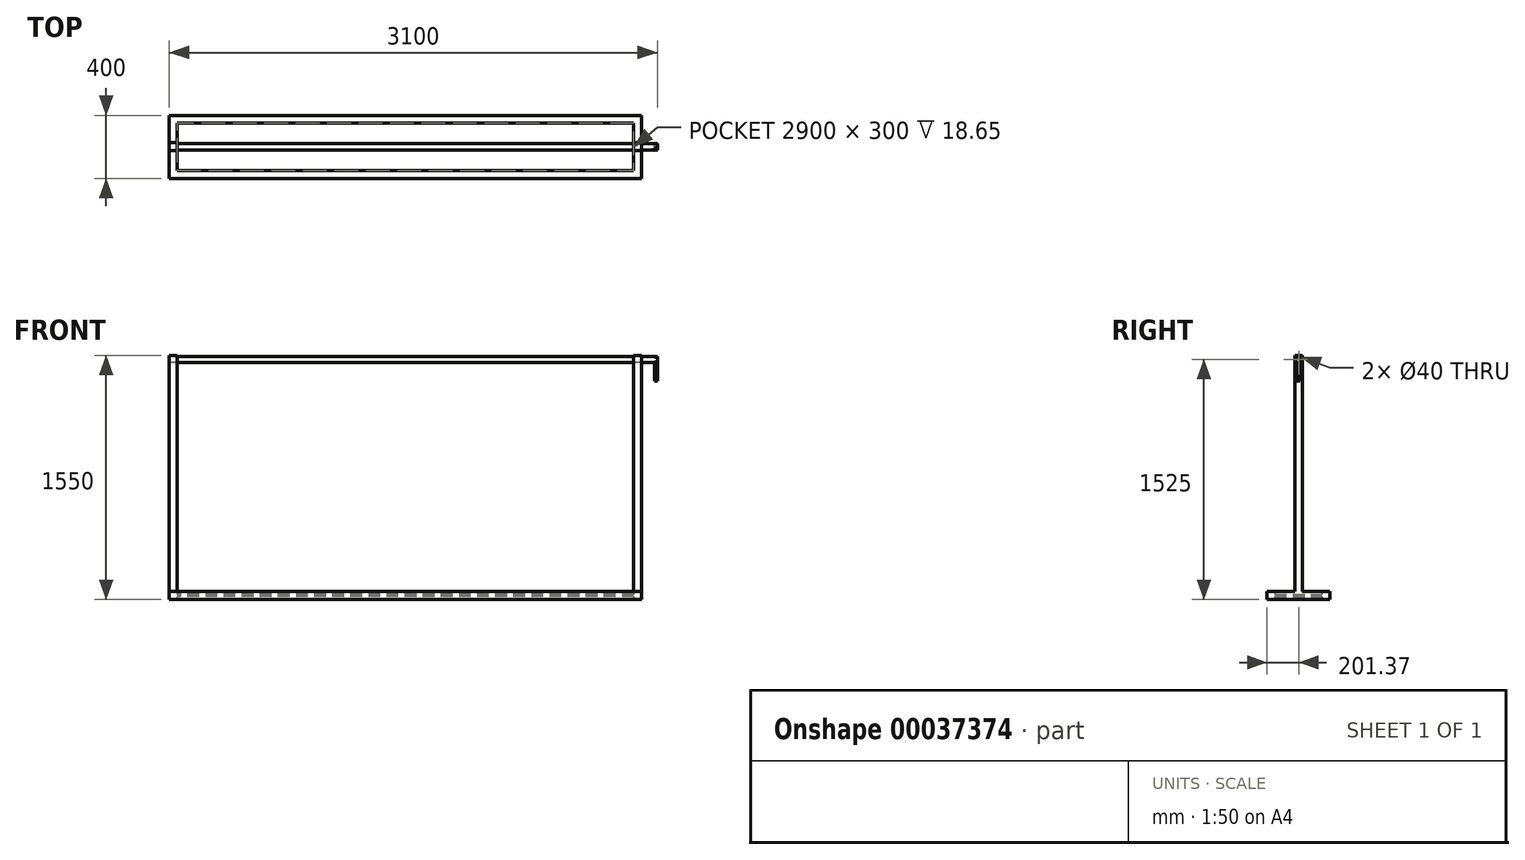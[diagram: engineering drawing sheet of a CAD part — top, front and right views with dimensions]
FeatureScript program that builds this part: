
annotation { "Feature Type Name" : "Feature", "Feature Type Description" : "" }
export const myFeature = defineFeature(function(context is Context, id is Id, definition is map)
    precondition{}
    {
        {
            var Q0;
            Q0=qCreatedBy(makeId("Top.planeOp"),FACE);
            var sketch = newSketch(context, id + "F0", { "sketchPlane" : qUnion([Q0])});
            skLineSegment(sketch, "E0.rect.bottom", {"start": v(1500, -200) * mm, "end": v(-1500, -200) * mm});
            skLineSegment(sketch, "E0.rect.top", {"start": v(1500, 200) * mm, "end": v(-1500, 200) * mm});
            skLineSegment(sketch, "E0.rect.left", {"start": v(1500, -200) * mm, "end": v(1500, 200) * mm});
            skLineSegment(sketch, "E0.rect.right", {"start": v(-1500, -200) * mm, "end": v(-1500, 200) * mm});
            skPoint(sketch, "E0.rect.middle", {"position": v(0, 0) * mm});
            skLineSegment(sketch, "E1.0", {"start": v(1450, -150) * mm, "end": v(-1450, -150) * mm});
            skLineSegment(sketch, "E2.0", {"start": v(-1450, -150) * mm, "end": v(-1450, 150) * mm});
            skLineSegment(sketch, "E3.0", {"start": v(1450, 150) * mm, "end": v(-1450, 150) * mm});
            skLineSegment(sketch, "E4.0", {"start": v(1450, -150) * mm, "end": v(1450, 150) * mm});
            skSolve(sketch);
        }
        {
            var Q0;
            Q0 = qSketchRegion(id + "F0", true);
            extrude(context, id + "F1", {"entities" : qUnion([Q0]), "endBound" : BoundingType.SYMMETRIC, "depth" : 50 * mm});
        }
        {
            var Q0;
            Q0=makeQuery(id+"F1.opExtrude","CAP_FACE",FACE,{"disambiguationData":[OSD([sQuery(id+"F0.wireOp",EDGE,"E0.rect.bottom"),sQuery(id+"F0.wireOp",EDGE,"E0.rect.top"),sQuery(id+"F0.wireOp",EDGE,"E0.rect.left"),sQuery(id+"F0.wireOp",EDGE,"E0.rect.right"),sQuery(id+"F0.wireOp",EDGE,"E1.0"),sQuery(id+"F0.wireOp",EDGE,"E2.0"),sQuery(id+"F0.wireOp",EDGE,"E3.0"),sQuery(id+"F0.wireOp",EDGE,"E4.0")])],"isStart":false});
            var sketch = newSketch(context, id + "F2", { "sketchPlane" : qUnion([Q0])});
            skPoint(sketch, "E5.MirrorP", {"position": v(1500, 0) * mm});
            skLineSegment(sketch, "E6", {"start": v(-1500, 0) * mm, "end": v(-1500, 26.37) * mm});
            skLineSegment(sketch, "E7.bottom", {"start": v(-1500, 26.37) * mm, "end": v(-1450, 26.37) * mm});
            skLineSegment(sketch, "E7.top", {"start": v(-1500, -23.63) * mm, "end": v(-1450, -23.63) * mm});
            skLineSegment(sketch, "E7.left", {"start": v(-1500, 26.37) * mm, "end": v(-1500, -23.63) * mm});
            skLineSegment(sketch, "E7.right", {"start": v(-1450, 26.37) * mm, "end": v(-1450, -23.63) * mm});
            skLineSegment(sketch, "E8.MirrorCS", {"start": v(1500, 0) * mm, "end": v(1500, 26.37) * mm});
            skLineSegment(sketch, "E9.MirrorCS", {"start": v(1500, 26.37) * mm, "end": v(1450, 26.37) * mm});
            skLineSegment(sketch, "E10.MirrorCS", {"start": v(1450, 26.37) * mm, "end": v(1450, -23.63) * mm});
            skLineSegment(sketch, "E11.MirrorCS", {"start": v(1500, -23.63) * mm, "end": v(1450, -23.63) * mm});
            skLineSegment(sketch, "E12.MirrorCS", {"start": v(1500, 26.37) * mm, "end": v(1500, -23.63) * mm});
            skSolve(sketch);
        }
        {
            var Q0;
            Q0 = qSketchRegion(id + "F2", true);
            extrude(context, id + "F3", {"entities" : qUnion([Q0]), "operationType" : NewBodyOperationType.ADD, "depth" : 1500 * mm});
        }
        {
            var Q0;
            Q0=makeQuery(id+"F3.boolean.opBoolean","MERGE",FACE,{"derivedFrom":[makeQuery(id+"F1.opExtrude","SWEPT_FACE",FACE,{"disambiguationData":[OSD([sQuery(id+"F0.wireOp",EDGE,"E0.rect.right")])]}),makeQuery(id+"F3.opExtrude","SWEPT_FACE",FACE,{"disambiguationData":[OSD([sQuery(id+"F2.wireOp",EDGE,"E7.left")])]})]});
            var sketch = newSketch(context, id + "F4", { "sketchPlane" : qUnion([Q0])});
            skCircle(sketch, "E13", {"center": v(-1.37, 1500) * mm, "radius": 20 * mm});
            skSolve(sketch);
        }
        {
            var Q0;
            Q0 = qSketchRegion(id + "F4", true);
            extrude(context, id + "F5", {"entities" : qUnion([Q0]), "operationType" : NewBodyOperationType.REMOVE, "oppositeDirection" : true, "depth" : 3064.82 * mm});
        }
        {
            var Q0;
            Q0=makeQuery(id+"F3.boolean.opBoolean","MERGE",FACE,{"derivedFrom":[makeQuery(id+"F1.opExtrude","SWEPT_FACE",FACE,{"disambiguationData":[OSD([sQuery(id+"F0.wireOp",EDGE,"E0.rect.right")])]}),makeQuery(id+"F3.opExtrude","SWEPT_FACE",FACE,{"disambiguationData":[OSD([sQuery(id+"F2.wireOp",EDGE,"E7.left")])]})]});
            var sketch = newSketch(context, id + "F6", { "sketchPlane" : qUnion([Q0])});
            skCircle(sketch, "E14", {"center": v(-1.37, 1500) * mm, "radius": 20 * mm});
            skPoint(sketch, "E14.first.point", {"position": v(-2.85, 1519.95) * mm});
            skPoint(sketch, "E14.second.point", {"position": v(0, 1480.05) * mm});
            skPoint(sketch, "E14.third.point", {"position": v(18.6, 1500.92) * mm});
            skSolve(sketch);
        }
        {
            var Q0;
            Q0 = qSketchRegion(id + "F6", true);
            var Q1;
            Q1=makeQuery(id+"F6.imprint","IMPRINT",FACE,{"disambiguationData":[TD([[makeQuery(id+"F6.imprint","IMPRINT",EDGE,{"derivedFrom":sQuery(id+"F6.wireOp",EDGE,"a49429df-8ac3-4c14-a87f-d7024776e782.0")}),1.0]])]});
            extrude(context, id + "F7", {"entities" : qUnion([Q0, Q1]), "oppositeDirection" : true, "depth" : 3100 * mm});
        }
        {
            var Q0;
            Q0=makeQuery(id+"F7.opExtrude","CAP_FACE",FACE,{"disambiguationData":[OSD([sQuery(id+"F6.wireOp",EDGE,"E14")])],"isStart":false});
            var sketch = newSketch(context, id + "F8", { "sketchPlane" : qUnion([Q0])});
            skLineSegment(sketch, "E15.rect.left", {"start": v(-10.64, 1364.54) * mm, "end": v(-9.46, 1420.97) * mm});
            skLineSegment(sketch, "E15.rect.right", {"start": v(7.72, 1364.54) * mm, "end": v(10.92, 1517.57) * mm});
            skPoint(sketch, "E15.rect.middle", {"position": v(1.37, 1500) * mm});
            skPoint(sketch, "E15.rect.top.end.orphan", {"position": v(13.38, 1635.46) * mm});
            skPoint(sketch, "E15.rect.top.start.orphan", {"position": v(-4.98, 1635.46) * mm});
            skLineSegment(sketch, "E16", {"start": v(7.72, 1364.54) * mm, "end": v(-10.64, 1364.54) * mm});
            skLineSegment(sketch, "E17", {"start": v(10.92, 1517.57) * mm, "end": v(-9.46, 1517.57) * mm});
            skLineSegment(sketch, "E18", {"start": v(-9.46, 1517.57) * mm, "end": v(-9.46, 1420.97) * mm});
            skSolve(sketch);
        }
        {
            var Q0;
            Q0 = qSketchRegion(id + "F8", true);
            extrude(context, id + "F9", {"entities" : qUnion([Q0]), "operationType" : NewBodyOperationType.ADD, "oppositeDirection" : true, "depth" : 18.8 * mm});
        }
        {
            var Q0;
            Q0=makeQuery(id+"F9.boolean.opBoolean","MERGE",FACE,{"derivedFrom":[makeQuery(id+"F7.opExtrude","CAP_FACE",FACE,{"disambiguationData":[OSD([sQuery(id+"F6.wireOp",EDGE,"E14")])],"isStart":false}),makeQuery(id+"F9.opExtrude","CAP_FACE",FACE,{"disambiguationData":[OSD([sQuery(id+"F8.wireOp",EDGE,"E15.rect.bottom"),sQuery(id+"F8.wireOp",EDGE,"E15.rect.top"),sQuery(id+"F8.wireOp",EDGE,"E15.rect.left"),sQuery(id+"F8.wireOp",EDGE,"E15.rect.right")])],"isStart":true})]});
            var sketch = newSketch(context, id + "F10", { "sketchPlane" : qUnion([Q0])});
            skPoint(sketch, "E19.centerSnap0", {"position": v(8.95, 1423.3) * mm});
            skCircle(sketch, "E20.0", {"center": v(0, 1378.42) * mm, "radius": 6.07 * mm});
            skSolve(sketch);
        }
        {
            var Q0;
            Q0=sQuery(id+"F10.wireOp",EDGE,"E20.0");
            extrude(context, id + "F11", {"bodyType" : ToolBodyType.SURFACE, "surfaceEntities" : qUnion([Q0]), "depth" : 101.6 * mm});
        }
        {
            var Q0;
            Q0=makeQuery(id+"F0.imprint","IMPRINT",FACE,{"disambiguationData":[TD([[makeQuery(id+"F0.imprint","IMPRINT",EDGE,{"derivedFrom":sQuery(id+"F0.wireOp",EDGE,"E1.0")}),-1.0]])]});
            extrude(context, id + "F12", {"entities" : qUnion([Q0]), "operationType" : NewBodyOperationType.ADD, "endBound" : BoundingType.SYMMETRIC, "depth" : 12.7 * mm});
        }
    });
